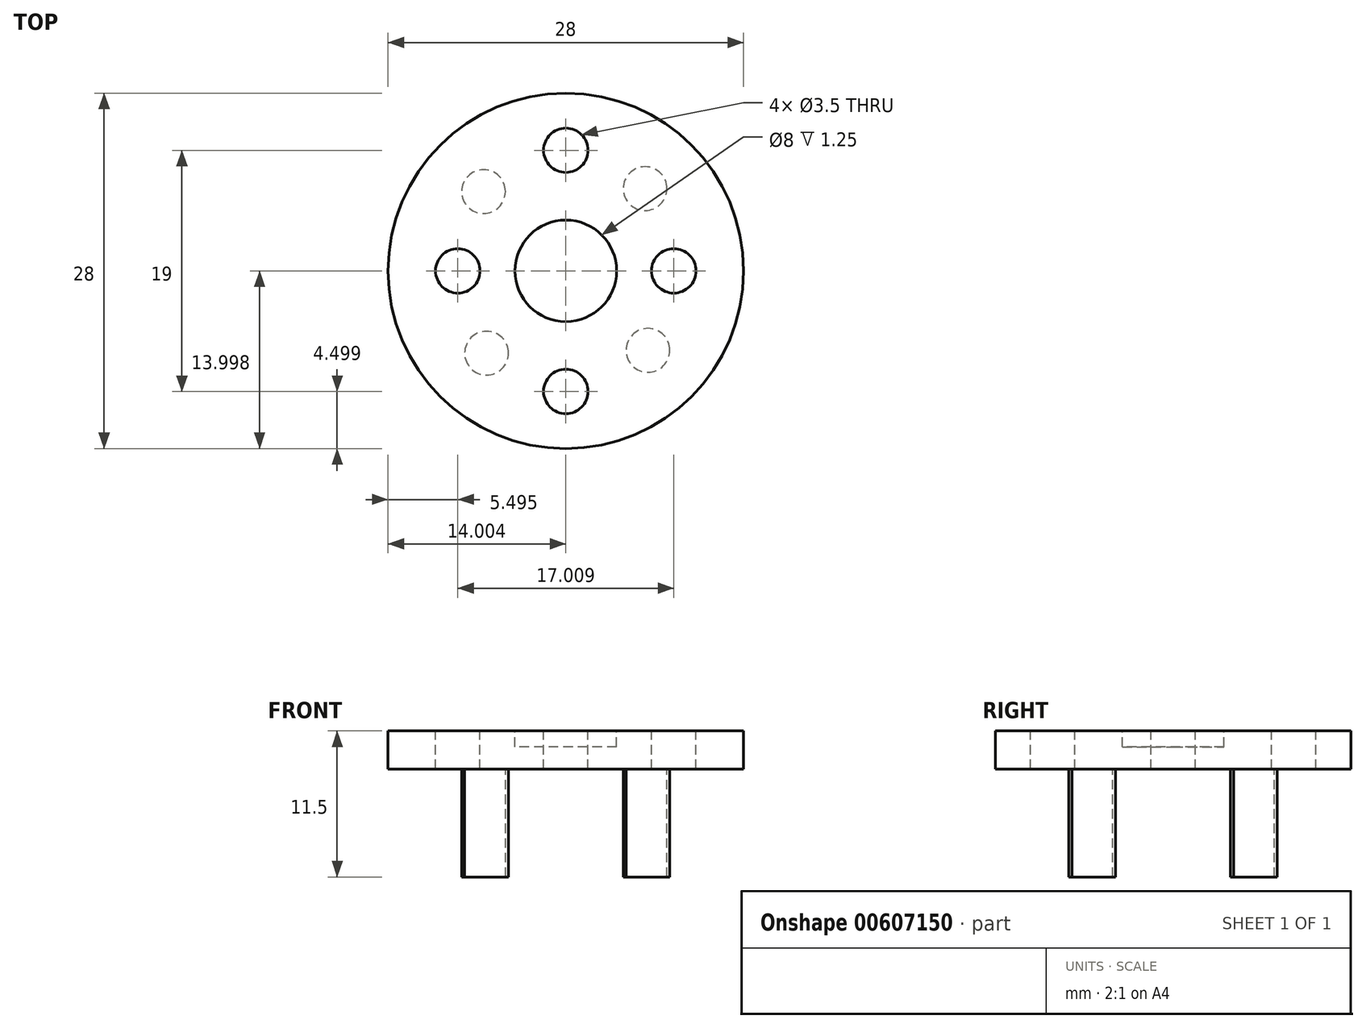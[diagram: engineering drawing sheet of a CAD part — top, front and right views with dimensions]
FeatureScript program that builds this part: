
annotation { "Feature Type Name" : "Feature", "Feature Type Description" : "" }
export const myFeature = defineFeature(function(context is Context, id is Id, definition is map)
    precondition{}
    {
        {
            var Q0;
            Q0=qCreatedBy(makeId("Top.planeOp"),FACE);
            var sketch = newSketch(context, id + "F0", { "sketchPlane" : qUnion([Q0])});
            skCircle(sketch, "E0", {"center": v(-41.54, -7.5) * mm, "radius": 14 * mm});
            skSolve(sketch);
        }
        {
            var Q0;
            Q0=makeQuery(id+"F0.imprint","IMPRINT",FACE,{"disambiguationData":[TD([[makeQuery(id+"F0.imprint","IMPRINT",EDGE,{"derivedFrom":sQuery(id+"F0.wireOp",EDGE,"E0")}),1.0]])]});
            extrude(context, id + "F1", {"entities" : qUnion([Q0]), "depth" : 3 * mm, "offsetDistance" : 25.4 * mm});
        }
        {
            var Q0;
            Q0=makeQuery(id+"F1.opExtrude","CAP_FACE",FACE,{"disambiguationData":[OSD([sQuery(id+"F0.wireOp",EDGE,"E0")])],"isStart":false});
            var sketch = newSketch(context, id + "F2", { "sketchPlane" : qUnion([Q0])});
            skCircle(sketch, "E1", {"center": v(-41.54, -7.5) * mm, "radius": 4 * mm});
            skSolve(sketch);
        }
        {
            var Q0;
            Q0=makeQuery(id+"F2.imprint","IMPRINT",FACE,{"disambiguationData":[TD([[makeQuery(id+"F2.imprint","IMPRINT",EDGE,{"derivedFrom":sQuery(id+"F2.wireOp",EDGE,"E1")}),1.0]])]});
            extrude(context, id + "F3", {"entities" : qUnion([Q0]), "operationType" : NewBodyOperationType.REMOVE, "oppositeDirection" : true, "depth" : 1.25 * mm, "offsetDistance" : 25.4 * mm});
        }
        {
            var Q0;
            Q0=makeQuery(id+"F1.opExtrude","CAP_FACE",FACE,{"disambiguationData":[OSD([sQuery(id+"F0.wireOp",EDGE,"E0")])],"isStart":false});
            var sketch = newSketch(context, id + "F4", { "sketchPlane" : qUnion([Q0])});
            skLineSegment(sketch, "E2", {"start": v(-41.54, -7.5) * mm, "end": v(-41.54, 2) * mm});
            skLineSegment(sketch, "E3", {"start": v(-41.54, -7.5) * mm, "end": v(-33.04, -7.5) * mm});
            skLineSegment(sketch, "E4", {"start": v(-41.54, -7.5) * mm, "end": v(-50.05, -7.5) * mm});
            skLineSegment(sketch, "E5", {"start": v(-41.54, -7.5) * mm, "end": v(-41.54, -17) * mm});
            skCircle(sketch, "E6", {"center": v(-41.54, 2) * mm, "radius": 1.75 * mm});
            skCircle(sketch, "E7", {"center": v(-33.04, -7.5) * mm, "radius": 1.75 * mm});
            skCircle(sketch, "E8", {"center": v(-41.54, -17) * mm, "radius": 1.75 * mm});
            skLineSegment(sketch, "E9", {"start": v(-41.54, -7.5) * mm, "end": v(-48.02, -1.26) * mm});
            skLineSegment(sketch, "E10", {"start": v(-41.54, -7.5) * mm, "end": v(-35.07, -13.76) * mm});
            skCircle(sketch, "E11", {"center": v(-48.02, -1.26) * mm, "radius": 1.73 * mm});
            skCircle(sketch, "E12", {"center": v(-35.07, -13.76) * mm, "radius": 1.73 * mm});
            skLineSegment(sketch, "E13", {"start": v(-41.54, -7.5) * mm, "end": v(-47.78, -13.98) * mm});
            skLineSegment(sketch, "E14", {"start": v(-41.54, -7.5) * mm, "end": v(-35.3, -1.02) * mm});
            skCircle(sketch, "E15", {"center": v(-47.78, -13.98) * mm, "radius": 1.73 * mm});
            skCircle(sketch, "E16", {"center": v(-35.3, -1.02) * mm, "radius": 1.73 * mm});
            skCircle(sketch, "E17", {"center": v(-50.05, -7.5) * mm, "radius": 1.75 * mm});
            skSolve(sketch);
        }
        {
            var Q0;
            Q0=makeQuery(id+"F4.imprint","IMPRINT",FACE,{"disambiguationData":[TD([[makeQuery(id+"F4.imprint","IMPRINT",EDGE,{"derivedFrom":sQuery(id+"F4.wireOp",EDGE,"E11")}),1.0]])]});
            var Q1;
            Q1=makeQuery(id+"F4.imprint","IMPRINT",FACE,{"disambiguationData":[TD([[makeQuery(id+"F4.imprint","IMPRINT",EDGE,{"derivedFrom":sQuery(id+"F4.wireOp",EDGE,"E12")}),1.0]])]});
            var Q2;
            Q2=makeQuery(id+"F4.imprint","IMPRINT",FACE,{"disambiguationData":[TD([[makeQuery(id+"F4.imprint","IMPRINT",EDGE,{"derivedFrom":sQuery(id+"F4.wireOp",EDGE,"E15")}),1.0]])]});
            var Q3;
            Q3=makeQuery(id+"F4.imprint","IMPRINT",FACE,{"disambiguationData":[TD([[makeQuery(id+"F4.imprint","IMPRINT",EDGE,{"derivedFrom":sQuery(id+"F4.wireOp",EDGE,"E16")}),1.0]])]});
            extrude(context, id + "F5", {"entities" : qUnion([Q0, Q1, Q2, Q3]), "operationType" : NewBodyOperationType.ADD, "oppositeDirection" : true, "depth" : 11.5 * mm, "offsetDistance" : 25.4 * mm});
        }
        {
            var Q0;
            Q0=makeQuery(id+"F4.imprint","IMPRINT",FACE,{"disambiguationData":[TD([[makeQuery(id+"F4.imprint","IMPRINT",EDGE,{"derivedFrom":sQuery(id+"F4.wireOp",EDGE,"T0dgnAG3-JtuG-JX6L-m1mJ-9RjSPBLAi7Wo")}),1.0]])]});
            var Q1;
            Q1=makeQuery(id+"F4.imprint","IMPRINT",FACE,{"disambiguationData":[TD([[makeQuery(id+"F4.imprint","IMPRINT",EDGE,{"derivedFrom":sQuery(id+"F4.wireOp",EDGE,"E6")}),1.0]])]});
            var Q2;
            Q2=makeQuery(id+"F4.imprint","IMPRINT",FACE,{"disambiguationData":[TD([[makeQuery(id+"F4.imprint","IMPRINT",EDGE,{"derivedFrom":sQuery(id+"F4.wireOp",EDGE,"E7")}),1.0]])]});
            var Q3;
            Q3=makeQuery(id+"F4.imprint","IMPRINT",FACE,{"disambiguationData":[TD([[makeQuery(id+"F4.imprint","IMPRINT",EDGE,{"derivedFrom":sQuery(id+"F4.wireOp",EDGE,"E8")}),1.0]])]});
            extrude(context, id + "F6", {"entities" : qUnion([Q0, Q1, Q2, Q3]), "operationType" : NewBodyOperationType.REMOVE, "oppositeDirection" : true, "depth" : 25.4 * mm, "offsetDistance" : 25.4 * mm});
        }
        {
            var Q0;
            Q0=makeQuery(id+"F4.imprint","IMPRINT",FACE,{"disambiguationData":[TD([[makeQuery(id+"F4.imprint","IMPRINT",EDGE,{"derivedFrom":sQuery(id+"F4.wireOp",EDGE,"E17")}),1.0]])]});
            extrude(context, id + "F7", {"entities" : qUnion([Q0]), "operationType" : NewBodyOperationType.REMOVE, "oppositeDirection" : true, "depth" : 25.4 * mm, "offsetDistance" : 25.4 * mm});
        }
    });
